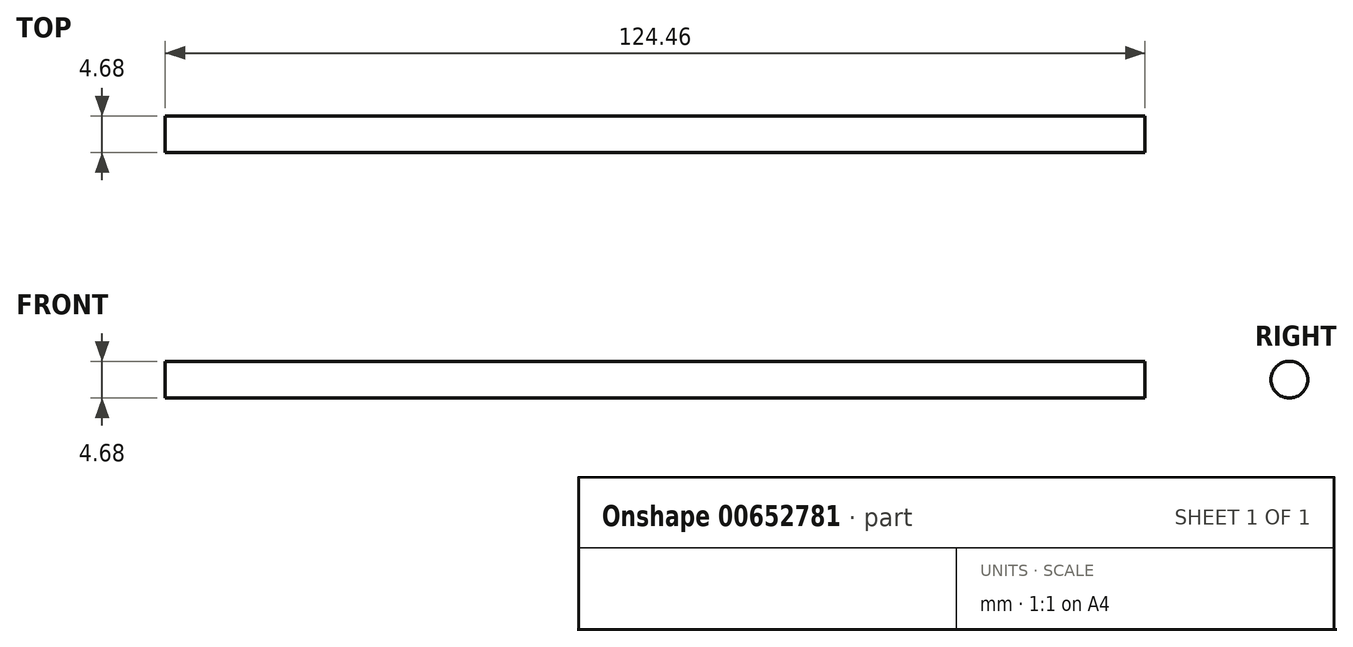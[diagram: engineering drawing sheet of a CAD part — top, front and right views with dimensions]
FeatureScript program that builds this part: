
annotation { "Feature Type Name" : "Feature", "Feature Type Description" : "" }
export const myFeature = defineFeature(function(context is Context, id is Id, definition is map)
    precondition{}
    {
        {
            var Q0;
            Q0=qCreatedBy(makeId("Right.planeOp"),FACE);
            var sketch = newSketch(context, id + "F0", { "sketchPlane" : qUnion([Q0])});
            skCircle(sketch, "E0", {"center": v(0, 0) * mm, "radius": 2.34 * mm});
            skSolve(sketch);
        }
        {
            var Q0;
            Q0=makeQuery(id+"F0.imprint","IMPRINT",FACE,{"disambiguationData":[TD([[makeQuery(id+"F0.imprint","IMPRINT",EDGE,{"derivedFrom":sQuery(id+"F0.wireOp",EDGE,"E0")}),1.0]])]});
            extrude(context, id + "F1", {"entities" : qUnion([Q0]), "depth" : 124.46 * mm, "offsetDistance" : 25.4 * mm});
        }
    });
